# Revit family: NLRS_33_GM_FB_TC_STORAX_vloerluik_CCA-GD_BCB
name_source: partatom
category: Generic Models
revit_build: Autodesk Revit 2014 (Build: 20130308_1515(x64)
units: mm (PartAtom-declared; Revit-internal decimal feet)

## types (5) — shared parameters
Manufacturer = Storax
Model = BV
URL = http://www.storax.nl
belasting = 15 kN
binnenluik = composiet aluminium
brandwerend 90 min = nee
gasdrukveer = ja
geïsoleerd = nee
materiaal = bcb_aluminium
productgroep = Vloerluiken
rubberen_afdichting = enkel
scharnierend = ja
sluiting hoek = Yes
vergrendeling = nee
vullen_met_beton = nee
zero-valued in all types: Default Elevation

## per-type parameters (varying)
| type | afstand scharnier | binnenmaat_breedte | binnenmaat_lengte | gewicht | sluiting | sluiting x-as | sluiting y-as | uitwendige_breedte | uitwendige_lengte |
| CCA-GD 66 | 72 mm | 580 mm  [stored 1.90289 ft] | 600 mm  [stored 1.9685 ft] | 13 | 2 | No | No | 720 mm  [stored 2.3622 ft] | 720 mm  [stored 2.3622 ft] |
| CCA-GD 86 | 202 mm  [stored 0.66273 ft] | 800 mm  [stored 2.62467 ft] | 600 mm  [stored 1.9685 ft] | 15 | 3 | No | Yes | 940 mm  [stored 3.08399 ft] | 720 mm  [stored 2.3622 ft] |
| CCA-GD 88 | 202 mm  [stored 0.66273 ft] | 800 mm  [stored 2.62467 ft] | 800 mm  [stored 2.62467 ft] | 18 | 5 | Yes | Yes | 940 mm  [stored 3.08399 ft] | 920 mm  [stored 3.01837 ft] |
| CCA-GD 106 | 202 mm  [stored 0.66273 ft] | 1000 mm  [stored 3.28084 ft] | 600 mm  [stored 1.9685 ft] | 18 | 3 | No | Yes | 1140 mm  [stored 3.74016 ft] | 720 mm  [stored 2.3622 ft] |
| maatwerk | 72 mm | 980 mm  [stored 3.21522 ft] | 600 mm  [stored 1.9685 ft] | 0 | 0 | Yes | Yes | 1120 mm  [stored 3.67454 ft] | 720 mm  [stored 2.3622 ft] |

note: [stored X ft] marks values corroborated as IEEE doubles in the binary element streams (Revit-internal decimal feet)

## geometry (parser evidence)
native form markers: Blend x768, Sweep x11
no freeform markers — native parametric forms only
